# Revit family: Солід
name_source: partatom
category: Оборудование
units: mm (PartAtom-declared; Revit-internal decimal feet)

## family parameters
Всегда вертикально = Да
Классификация = Нет
На основе рабочей плоскости = Нет
Общий = Нет
При загрузке вырезать с полостями = Нет
Размер круглого соединителя = Использовать диаметр
Тип детали = Нормальный
Точка принадлежности помещению = Нет

## types (4) — shared parameters
00_20_Виробник = Вентс
00_20_Назва = Осьовий вентилятор
L1 = 38 мм
URL = https://vents.ua
Изготовитель = Вентс
Класифікація навантаження = HVAC
Кількість фаз = 1
Матеріал зони обслуговуваня = <По категории>
Матеріал корпусу = Пластмаса, непрозора, біла
Напруга = 230 В
Струм = 0 А
zero-valued in all types: Отметка по умолчанию

## per-type parameters (varying)
| type | B | D | Dy | H | L | L2 | Вага | Висота | Довжина | Діаметр | Максимальний потік повітря | Потужність | Рівень звукового тиску на відстані 3 м | Частота | Ширина |
| 100 Солід | 160 мм | 100 мм | 95 мм | 160 мм | 79 мм | 41 мм | 0.51 кг | 160 мм | 79 мм | 100 мм | 85.0 м³/ч | 8 Вт | 27 дБА | 50 Гц | 160 мм |
| 125 Солід | 180 мм | 125 мм | 120 мм | 180 мм | 85 мм | 47 мм | 0.75 кг | 180 мм | 85 мм | 125 мм | 155.0 м³/ч | 18 Вт | 32 дБА | 50 Гц | 180 мм |
| 100 Солід (220 В/60 Гц) | 160 мм | 100 мм | 95 мм | 160 мм | 79 мм | 41 мм | 0.51 кг | 160 мм | 79 мм | 100 мм | 85.0 м³/ч | 8 Вт | 27 дБА | 60 Гц | 160 мм |
| 125 Солід (220 В/60 Гц) | 180 мм | 125 мм | 120 мм | 180 мм | 85 мм | 47 мм | 0.75 кг | 180 мм | 85 мм | 125 мм | 155.0 м³/ч | 18 Вт | 32 дБА | 60 Гц | 180 мм |

note: column(s) folded — value = type name in every type: 00_20_Тип
